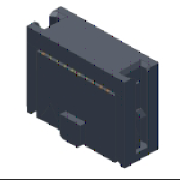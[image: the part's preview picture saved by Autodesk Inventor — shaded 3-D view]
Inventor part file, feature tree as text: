
AUTODESK INVENTOR PART (.ipt)
format: ipt  version: 2017 (Build 210142000, 142)  size: 581,632 bytes
history: native  units: in
note: dims shown in document units (in); Inventor stores cm internally (conversion verified against a paired STEP export)
features: sketch x12, extrude x10, projected_geometry x3, other x2, plane x1
ambient origin geometry x8: Origin, YZ Plane, XZ Plane, XY Plane, X Axis, Y Axis, Z Axis, Center Point
bodies: Solid1 (feature_tree)
feature tree (28):
  extrude  "Extrusion1"  Depth=0.0354in
  extrude  "Extrusion2"  Depth=0.1417in
  extrude  "Extrusion3"  TaperAngle=135.0deg  [1 undecoded]
  extrude  "Extrusion4"  Depth=0.0197in
  extrude  "Extrusion5"  Depth=0.0394in TaperAngle=0.0deg
  extrude  "Extrusion6"  Depth=0.048in
  extrude  "Extrusion7"  Depth=0.0591in
  plane  "Work Plane1"
  extrude  "Extrusion8"  Depth=0.0346in
  extrude  "Extrusion9"  Depth=0.0655in
  extrude  "Extrusion10"  Depth=0.0394in
  sketch  "Sketch20"  dims[d38=0.0098in]
  sketch  "Sketch21"  dims[d39=0.0394in d40=0.0098in d41=0.0394in d42=0.0in d43=0.0655in d44=0.8496in d45=0.0394in d46=0.0394in d47=0.0098in d48=0.0098in d49=0.0394in d50=0.0in d61=0.0197in d62=0.1575in d63=0.0039in d64=0.0in d65=0.0295in d66=0.1in d67=0.06in d68=0.1181in d69=0.0in d70=0.0197in d71=0.0787in d72=45.0deg d73=3.1496in d75=0.1in d90=0.0984in d91=0.0in d123=0.0004in d126=0.0004in d148=0.0004in d152=0.0004in d157=0.4213in d158=0.0in d160=0.0787in d161=0.0335in d162=0.1181in d163=0.3869in d164=0.0051in d165=0.9823in d166=0.0004in d167=0.0004in d168=0.0004in d169=0.0004in d170=0.0004in d171=0.0004in d172=0.0004in d173=0.0004in d174=0.0004in d175=0.0004in d177=0.0004in d178=0.2386in d179=0.0in d180=0.0004in d181=0.0047in d182=0.0004in d183=0.0047in d185=0.0394in d186=0.0787in d187=45.0deg d188=0.0689in d189=0.0787in d190=45.0deg d191=0.4217in d192=0.0012in d193=45.0deg d194=0.4217in d195=0.0012in d196=45.0deg d203=0.0197in d204=0.0012in d205=45.0deg d234=0.4213in d240=0.0098in d241=0.0098in d242=0.0098in d243=0.0659in d247=0.375in d248=25.1969in d250=0.05in d251=0.3937in d253=0.3937in]
  other  "Work Point1"
  other  "Work Point2"
  sketch  "Sketch1"  dims[d0=0.8496in d1=0.2362in d4=0.0354in d5=0.0295in d6=0.0236in d8=0.0295in d9=0.0236in d10=0.2362in d12=0.0354in]
  sketch  "Sketch2"  dims[d13=0.4016in d14=0.0in d15=0.1417in]
  sketch  "Sketch3"  dims[d17=0.0197in d19=135.0deg]
  sketch  "Sketch4"  dims[d20=135.0deg d21=0.0197in]
  sketch  "Sketch5"  dims[d22=0.1417in d23=0.0394in d24=0.0in]
  sketch  "Sketch6"  dims[d25=0.8496in d26=0.048in]
  sketch  "Sketch7"  dims[d28=0.0394in d29=0.0591in]
  sketch  "Sketch8"  dims[d30=0.0346in d31=0.0098in]
  sketch  "Sketch10"  dims[d32=0.0394in d33=0.0in d34=0.0655in]
  projected_geometry  "Projected Loop2"
  projected_geometry  "Projected Loop3"
  sketch  "Sketch12"  dims[d35=0.8496in d36=0.0394in]
  projected_geometry  "Projected Loop4"
note: 1 required parameter value undecoded (feature->parameter linkage not recoverable at this tier; creation-order binding heuristic only, values carry confidence <= 0.55)
